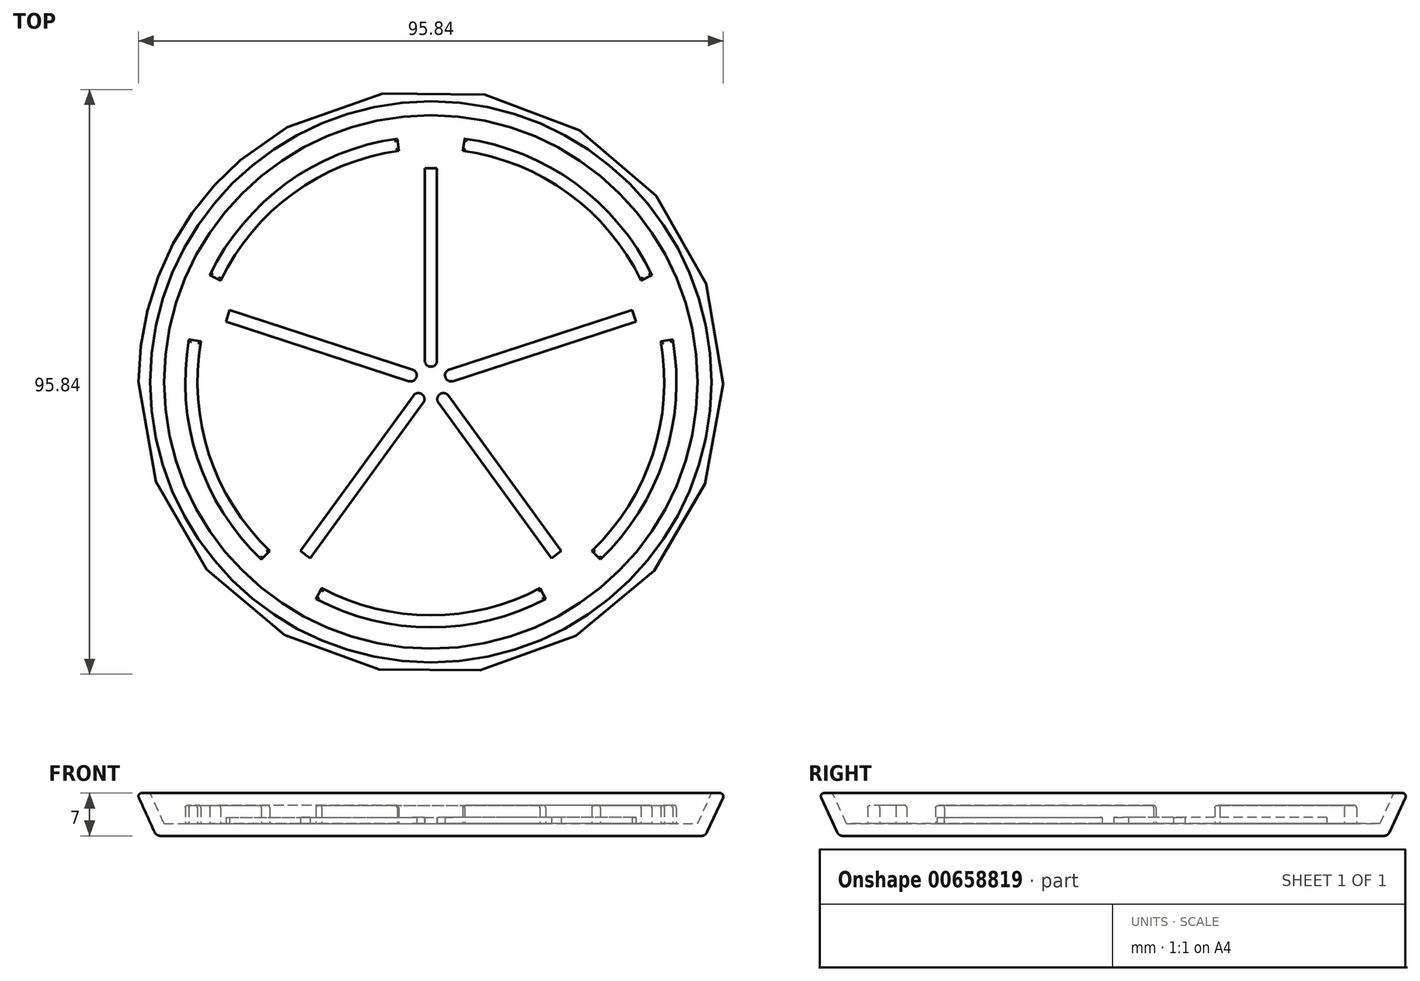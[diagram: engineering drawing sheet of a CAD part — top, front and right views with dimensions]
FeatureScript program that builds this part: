
annotation { "Feature Type Name" : "Feature", "Feature Type Description" : "" }
export const myFeature = defineFeature(function(context is Context, id is Id, definition is map)
    precondition{}
    {
        {
            var Q0;
            Q0=qCreatedBy(makeId("Right.planeOp"),FACE);
            var sketch = newSketch(context, id + "F0", { "sketchPlane" : qUnion([Q0])});
            skLineSegment(sketch, "E0", {"start": v(0, 0) * mm, "end": v(0, 2) * mm});
            skLineSegment(sketch, "E1", {"start": v(0, 2) * mm, "end": v(-43.72, 2) * mm});
            skLineSegment(sketch, "E2", {"start": v(-43.72, 2) * mm, "end": v(-46, 7) * mm});
            skLineSegment(sketch, "E3", {"start": v(-46, 7) * mm, "end": v(-48.2, 7) * mm});
            skLineSegment(sketch, "E4", {"start": v(-48.2, 7) * mm, "end": v(-45, 0) * mm});
            skLineSegment(sketch, "E5", {"start": v(-45, 0) * mm, "end": v(0, 0) * mm});
            skSolve(sketch);
        }
        {
            var Q0;
            Q0 = qSketchRegion(id + "F0", true);
            var Q1;
            Q1=sQuery(id+"F0.wireOp",EDGE,"E0");
            revolve(context, id + "F1", {"entities" : qUnion([Q0]), "axis" : qUnion([Q1]), "revolveType" : RevolveType.FULL});
        }
        {
            var Q0;
            Q0=makeQuery(id+"F1.opRevolve","SWEPT_EDGE",EDGE,{"disambiguationData":[OSD([sQuery(id+"F0.wireOp",EDGE,"E4"),sQuery(id+"F0.wireOp",EDGE,"E5")])]});
            fillet(context, id + "F2", {"entities" : qUnion([Q0]), "radius" : 1 * mm, "tangentPropagation" : true, "allowEdgeOverflow" : false});
        }
        {
            var Q0;
            Q0=makeQuery(id+"F1.opRevolve","SWEPT_EDGE",EDGE,{"disambiguationData":[OSD([sQuery(id+"F0.wireOp",EDGE,"E3"),sQuery(id+"F0.wireOp",EDGE,"E4")])]});
            fillet(context, id + "F3", {"entities" : qUnion([Q0]), "radius" : .5 * mm, "tangentPropagation" : true, "allowEdgeOverflow" : false});
        }
        {
            var Q0;
            Q0=makeQuery(id+"F1.opRevolve","SWEPT_FACE",FACE,{"disambiguationData":[OSD([sQuery(id+"F0.wireOp",EDGE,"E1")])]});
            var sketch = newSketch(context, id + "F4", { "sketchPlane" : qUnion([Q0])});
            skLineSegment(sketch, "E6.bottom", {"start": v(-1, 35) * mm, "end": v(1, 35) * mm});
            skLineSegment(sketch, "E6.left", {"start": v(-1, 35) * mm, "end": v(-1, 3.5) * mm});
            skLineSegment(sketch, "E6.right", {"start": v(1, 35) * mm, "end": v(1, 3.5) * mm});
            skArc(sketch, "E7", {"start": v(-1, 3.5) * mm, "mid": v(0, 2.5) * mm, "end": v(1, 3.5) * mm});
            skArc(sketch, "E8.1.0", {"start": v(-3.64, 0.13) * mm, "mid": v(-2.38, 0.77) * mm, "end": v(-3.02, 2.03) * mm});
            skLineSegment(sketch, "E8.1.1", {"start": v(-32.98, 11.77) * mm, "end": v(-3.02, 2.03) * mm});
            skLineSegment(sketch, "E8.1.2", {"start": v(-33.6, 9.86) * mm, "end": v(-3.64, 0.13) * mm});
            skArc(sketch, "E8.2.0", {"start": v(-1.25, -3.42) * mm, "mid": v(-1.47, -2.02) * mm, "end": v(-2.86, -2.24) * mm});
            skLineSegment(sketch, "E8.2.1", {"start": v(-21.38, -27.73) * mm, "end": v(-2.86, -2.24) * mm});
            skLineSegment(sketch, "E8.2.2", {"start": v(-19.76, -28.9) * mm, "end": v(-1.25, -3.42) * mm});
            skArc(sketch, "E8.3.0", {"start": v(2.86, -2.24) * mm, "mid": v(1.47, -2.02) * mm, "end": v(1.25, -3.42) * mm});
            skLineSegment(sketch, "E8.3.1", {"start": v(19.76, -28.9) * mm, "end": v(1.25, -3.42) * mm});
            skLineSegment(sketch, "E8.3.2", {"start": v(21.38, -27.73) * mm, "end": v(2.86, -2.24) * mm});
            skArc(sketch, "E8.4.0", {"start": v(3.02, 2.03) * mm, "mid": v(2.38, 0.77) * mm, "end": v(3.64, 0.13) * mm});
            skLineSegment(sketch, "E8.4.1", {"start": v(33.6, 9.86) * mm, "end": v(3.64, 0.13) * mm});
            skLineSegment(sketch, "E8.4.2", {"start": v(32.98, 11.77) * mm, "end": v(3.02, 2.03) * mm});
            skPoint(sketch, "E8.center", {"position": v(0, 0) * mm});
            skLineSegment(sketch, "E9.1.0", {"start": v(-33.6, 9.86) * mm, "end": v(-32.98, 11.77) * mm});
            skLineSegment(sketch, "E9.2.0", {"start": v(-19.76, -28.9) * mm, "end": v(-21.38, -27.73) * mm});
            skLineSegment(sketch, "E9.3.0", {"start": v(21.38, -27.73) * mm, "end": v(19.76, -28.9) * mm});
            skLineSegment(sketch, "E9.4.0", {"start": v(32.98, 11.77) * mm, "end": v(33.6, 9.86) * mm});
            skSolve(sketch);
        }
        {
            var Q0;
            Q0 = qSketchRegion(id + "F4", true);
            extrude(context, id + "F5", {"entities" : qUnion([Q0]), "operationType" : NewBodyOperationType.ADD, "depth" : 1 * mm, "offsetDistance" : 25 * mm});
        }
        {
            var Q0;
            Q0=makeQuery(id+"F1.opRevolve","SWEPT_FACE",FACE,{"disambiguationData":[OSD([sQuery(id+"F0.wireOp",EDGE,"E1")])]});
            var sketch = newSketch(context, id + "F6", { "sketchPlane" : qUnion([Q0])});
            skArc(sketch, "E10", {"start": v(-5.25, 37.89) * mm, "mid": v(-22.52, 30.92) * mm, "end": v(-34.45, 16.63) * mm});
            skArc(sketch, "E11.0", {"start": v(-5.53, 39.87) * mm, "mid": v(-23.7, 32.54) * mm, "end": v(-36.25, 17.5) * mm});
            skArc(sketch, "E12.cCircle", {"start": v(-5.53, 39.87) * mm, "mid": v(-23.7, 32.54) * mm, "end": v(-36.25, 17.5) * mm, "construction": true});
            skPoint(sketch, "E12.0.midPoint", {"position": v(0, 40.25) * mm});
            skLineSegment(sketch, "E13", {"start": v(-36.25, 17.5) * mm, "end": v(-34.45, 16.63) * mm});
            skLineSegment(sketch, "E14", {"start": v(-5.53, 39.87) * mm, "end": v(-5.25, 37.89) * mm});
            skLineSegment(sketch, "E15", {"start": v(5.53, 39.87) * mm, "end": v(5.25, 37.89) * mm});
            skLineSegment(sketch, "E16", {"start": v(36.25, 17.5) * mm, "end": v(34.45, 16.63) * mm});
            skLineSegment(sketch, "E17", {"start": v(39.64, 6.98) * mm, "end": v(37.67, 6.63) * mm});
            skLineSegment(sketch, "E18", {"start": v(26.4, -27.68) * mm, "end": v(27.78, -29.12) * mm});
            skLineSegment(sketch, "E19", {"start": v(17.88, -33.82) * mm, "end": v(18.8, -35.58) * mm});
            skLineSegment(sketch, "E20", {"start": v(-18.8, -35.58) * mm, "end": v(-17.88, -33.82) * mm});
            skLineSegment(sketch, "E21", {"start": v(-27.78, -29.12) * mm, "end": v(-26.4, -27.68) * mm});
            skLineSegment(sketch, "E22", {"start": v(-39.64, 6.98) * mm, "end": v(-37.67, 6.63) * mm});
            skArc(sketch, "E23.trimOffspring", {"start": v(-37.67, 6.63) * mm, "mid": v(-36.34, -11.94) * mm, "end": v(-26.4, -27.68) * mm});
            skArc(sketch, "E24.trimOffspring", {"start": v(-39.64, 6.98) * mm, "mid": v(-38.24, -12.56) * mm, "end": v(-27.78, -29.12) * mm, "construction": true});
            skArc(sketch, "E25.trimOffspring", {"start": v(-39.64, 6.98) * mm, "mid": v(-38.24, -12.56) * mm, "end": v(-27.78, -29.12) * mm});
            skArc(sketch, "E26.trimOffspring", {"start": v(36.25, 17.5) * mm, "mid": v(23.7, 32.54) * mm, "end": v(5.53, 39.87) * mm, "construction": true});
            skArc(sketch, "E27.trimOffspring", {"start": v(34.45, 16.63) * mm, "mid": v(22.52, 30.92) * mm, "end": v(5.25, 37.89) * mm});
            skArc(sketch, "E28.trimOffspring", {"start": v(36.25, 17.5) * mm, "mid": v(23.7, 32.54) * mm, "end": v(5.53, 39.87) * mm});
            skArc(sketch, "E29.trimOffspring", {"start": v(27.78, -29.12) * mm, "mid": v(38.24, -12.56) * mm, "end": v(39.64, 6.98) * mm, "construction": true});
            skArc(sketch, "E30.trimOffspring", {"start": v(26.4, -27.68) * mm, "mid": v(36.34, -11.94) * mm, "end": v(37.67, 6.63) * mm});
            skArc(sketch, "E31.trimOffspring", {"start": v(27.78, -29.12) * mm, "mid": v(38.24, -12.56) * mm, "end": v(39.64, 6.98) * mm});
            skArc(sketch, "E32.trimOffspring", {"start": v(-17.88, -33.82) * mm, "mid": v(0, -38.25) * mm, "end": v(17.88, -33.82) * mm});
            skArc(sketch, "E33.trimOffspring", {"start": v(-18.8, -35.58) * mm, "mid": v(0, -40.25) * mm, "end": v(18.8, -35.58) * mm, "construction": true});
            skArc(sketch, "E34.trimOffspring", {"start": v(-18.8, -35.58) * mm, "mid": v(0, -40.25) * mm, "end": v(18.8, -35.58) * mm});
            skPoint(sketch, "E35", {"position": v(0, -38.25) * mm});
            skSolve(sketch);
        }
        {
            var Q0;
            Q0 = qSketchRegion(id + "F6", true);
            extrude(context, id + "F7", {"entities" : qUnion([Q0]), "operationType" : NewBodyOperationType.ADD, "depth" : 3 * mm, "offsetDistance" : 25 * mm});
        }
        {
            var Q0;
            Q0=makeQuery(id+"F7.opExtrude","CAP_EDGE",EDGE,{"disambiguationData":[OSD([sQuery(id+"F6.wireOp",EDGE,"E10")])],"isStart":false});
            var Q1;
            Q1=makeQuery(id+"F7.opExtrude","CAP_EDGE",EDGE,{"disambiguationData":[OSD([sQuery(id+"F6.wireOp",EDGE,"E11.0")])],"isStart":false});
            var Q2;
            Q2=makeQuery(id+"F7.opExtrude","CAP_EDGE",EDGE,{"disambiguationData":[OSD([sQuery(id+"F6.wireOp",EDGE,"E13")])],"isStart":false});
            var Q3;
            Q3=makeQuery(id+"F7.opExtrude","CAP_EDGE",EDGE,{"disambiguationData":[OSD([sQuery(id+"F6.wireOp",EDGE,"E14")])],"isStart":false});
            var Q4;
            Q4=makeQuery(id+"F7.opExtrude","CAP_EDGE",EDGE,{"disambiguationData":[OSD([sQuery(id+"F6.wireOp",EDGE,"E22")])],"isStart":false});
            var Q5;
            Q5=makeQuery(id+"F7.opExtrude","CAP_EDGE",EDGE,{"disambiguationData":[OSD([sQuery(id+"F6.wireOp",EDGE,"E25.trimOffspring")])],"isStart":false});
            var Q6;
            Q6=makeQuery(id+"F7.opExtrude","CAP_EDGE",EDGE,{"disambiguationData":[OSD([sQuery(id+"F6.wireOp",EDGE,"E23.trimOffspring")])],"isStart":false});
            var Q7;
            Q7=makeQuery(id+"F7.opExtrude","CAP_EDGE",EDGE,{"disambiguationData":[OSD([sQuery(id+"F6.wireOp",EDGE,"E21")])],"isStart":false});
            var Q8;
            Q8=makeQuery(id+"F7.opExtrude","CAP_EDGE",EDGE,{"disambiguationData":[OSD([sQuery(id+"F6.wireOp",EDGE,"E20")])],"isStart":false});
            var Q9;
            Q9=makeQuery(id+"F7.opExtrude","CAP_EDGE",EDGE,{"disambiguationData":[OSD([sQuery(id+"F6.wireOp",EDGE,"E34.trimOffspring")])],"isStart":false});
            var Q10;
            Q10=makeQuery(id+"F7.opExtrude","CAP_EDGE",EDGE,{"disambiguationData":[OSD([sQuery(id+"F6.wireOp",EDGE,"E19")])],"isStart":false});
            var Q11;
            Q11=makeQuery(id+"F7.opExtrude","CAP_EDGE",EDGE,{"disambiguationData":[OSD([sQuery(id+"F6.wireOp",EDGE,"E32.trimOffspring")])],"isStart":false});
            var Q12;
            Q12=makeQuery(id+"F7.opExtrude","CAP_EDGE",EDGE,{"disambiguationData":[OSD([sQuery(id+"F6.wireOp",EDGE,"E31.trimOffspring")])],"isStart":false});
            var Q13;
            Q13=makeQuery(id+"F7.opExtrude","CAP_EDGE",EDGE,{"disambiguationData":[OSD([sQuery(id+"F6.wireOp",EDGE,"E30.trimOffspring")])],"isStart":false});
            var Q14;
            Q14=makeQuery(id+"F7.opExtrude","CAP_EDGE",EDGE,{"disambiguationData":[OSD([sQuery(id+"F6.wireOp",EDGE,"E18")])],"isStart":false});
            var Q15;
            Q15=makeQuery(id+"F7.opExtrude","CAP_FACE",FACE,{"disambiguationData":[OSD([sQuery(id+"F6.wireOp",EDGE,"E17"),sQuery(id+"F6.wireOp",EDGE,"E18"),sQuery(id+"F6.wireOp",EDGE,"E30.trimOffspring"),sQuery(id+"F6.wireOp",EDGE,"E31.trimOffspring")])],"isStart":false});
            var Q16;
            Q16=makeQuery(id+"F7.opExtrude","CAP_EDGE",EDGE,{"disambiguationData":[OSD([sQuery(id+"F6.wireOp",EDGE,"E28.trimOffspring")])],"isStart":false});
            var Q17;
            Q17=makeQuery(id+"F7.opExtrude","CAP_EDGE",EDGE,{"disambiguationData":[OSD([sQuery(id+"F6.wireOp",EDGE,"E16")])],"isStart":false});
            var Q18;
            Q18=makeQuery(id+"F7.opExtrude","CAP_EDGE",EDGE,{"disambiguationData":[OSD([sQuery(id+"F6.wireOp",EDGE,"E15")])],"isStart":false});
            var Q19;
            Q19=makeQuery(id+"F7.opExtrude","CAP_EDGE",EDGE,{"disambiguationData":[OSD([sQuery(id+"F6.wireOp",EDGE,"E27.trimOffspring")])],"isStart":false});
            fillet(context, id + "F8", {"entities" : qUnion([Q0, Q1, Q2, Q3, Q4, Q5, Q6, Q7, Q8, Q9, Q10, Q11, Q12, Q13, Q14, Q15, Q16, Q17, Q18, Q19]), "radius" : 0.4 * mm, "tangentPropagation" : true, "allowEdgeOverflow" : false});
        }
    });
